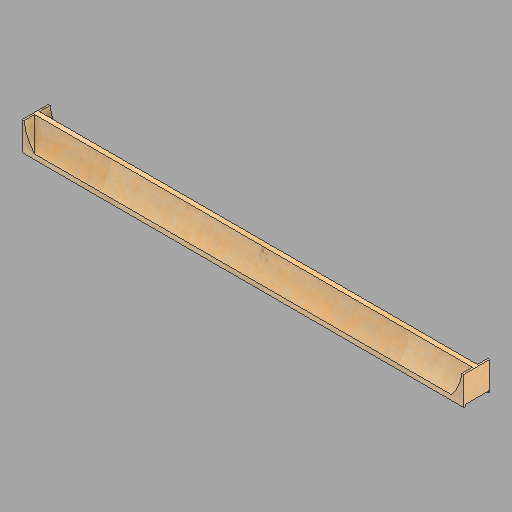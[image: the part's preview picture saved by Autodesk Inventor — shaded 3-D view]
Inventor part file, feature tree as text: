
AUTODESK INVENTOR PART (.ipt)
format: ipt  version: 2022.2 (Build 262287010, 287A)  size: 178,688 bytes
history: native  units: in
note: dims shown in document units (in); Inventor stores cm internally (conversion verified against a paired STEP export)
features: direct_edit x1, other x1, revolve x1
ambient origin geometry x8: Origin, YZ Plane, XZ Plane, XY Plane, X Axis, Y Axis, Z Axis, Center Point
bodies: Solid1 (feature_tree)
feature tree (3):
  direct_edit  "Direct Edit1"
  other  "Transom (2)"
  revolve  "Rotate1"  [1 undecoded]
note: 1 required parameter value undecoded (feature->parameter linkage not recoverable at this tier; creation-order binding heuristic only, values carry confidence <= 0.55)
